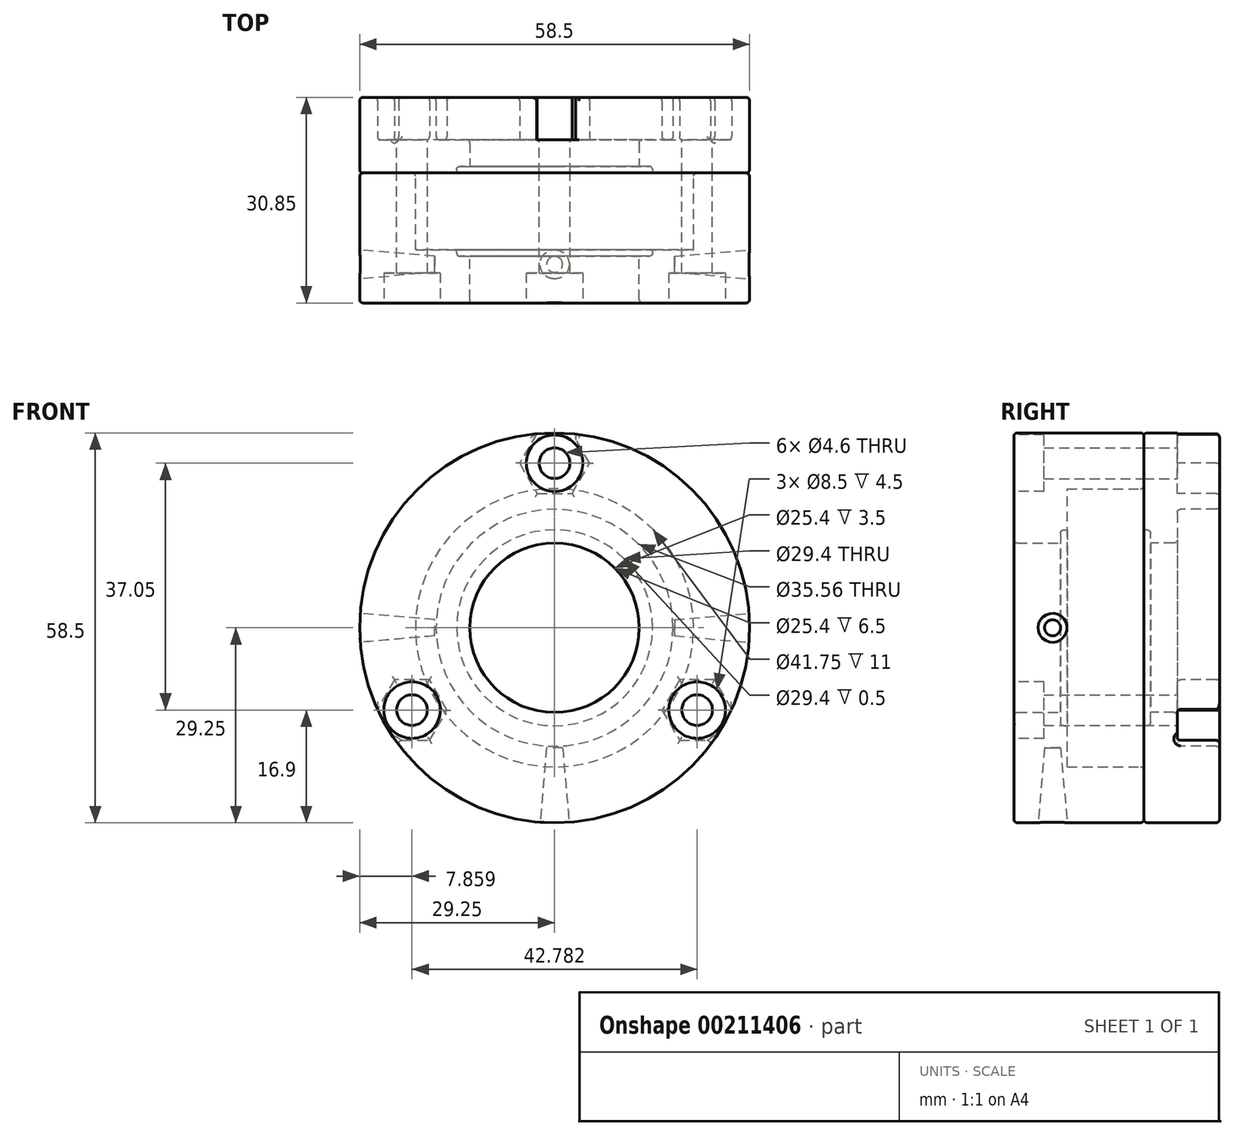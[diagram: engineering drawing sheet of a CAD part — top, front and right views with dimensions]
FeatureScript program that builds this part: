
annotation { "Feature Type Name" : "Feature", "Feature Type Description" : "" }
export const myFeature = defineFeature(function(context is Context, id is Id, definition is map)
    precondition{}
    {
        {
            var Q0;
            Q0=qCreatedBy(makeId("Front.planeOp"),FACE);
            var sketch = newSketch(context, id + "F0", { "sketchPlane" : qUnion([Q0])});
            skCircle(sketch, "E0", {"center": v(0, 0) * mm, "radius": 20.88 * mm});
            skCircle(sketch, "E1", {"center": v(0, 0) * mm, "radius": 29.25 * mm});
            skSolve(sketch);
        }
        {
            var Q0;
            Q0 = qSketchRegion(id + "F0", true);
            extrude(context, id + "F1", {"entities" : qUnion([Q0]), "depth" : 11.5 * mm});
        }
        {
            var Q0;
            Q0=makeQuery(id+"F1.opExtrude","CAP_FACE",FACE,{"disambiguationData":[OSD([sQuery(id+"F0.wireOp",EDGE,"E0"),sQuery(id+"F0.wireOp",EDGE,"E1")])],"isStart":false});
            var sketch = newSketch(context, id + "F2", { "sketchPlane" : qUnion([Q0])});
            skCircle(sketch, "E2.0", {"center": v(0, 0) * mm, "radius": 29.25 * mm});
            skCircle(sketch, "E3", {"center": v(0, 0) * mm, "radius": 12.7 * mm});
            skSolve(sketch);
        }
        {
            var Q0;
            Q0 = qSketchRegion(id + "F2", true);
            extrude(context, id + "F3", {"entities" : qUnion([Q0]), "operationType" : NewBodyOperationType.ADD, "depth" : 8 * mm});
        }
        {
            var Q0;
            Q0=makeQuery(id+"F1.opExtrude","CAP_FACE",FACE,{"disambiguationData":[OSD([sQuery(id+"F0.wireOp",EDGE,"E0"),sQuery(id+"F0.wireOp",EDGE,"E1")])],"isStart":true});
            var sketch = newSketch(context, id + "F4", { "sketchPlane" : qUnion([Q0])});
            skCircle(sketch, "E4.0", {"center": v(0, 0) * mm, "radius": 29.25 * mm});
            skCircle(sketch, "E5.0", {"center": v(0, 0) * mm, "radius": 12.7 * mm});
            skSolve(sketch);
        }
        {
            var Q0;
            Q0 = qSketchRegion(id + "F4", true);
            extrude(context, id + "F5", {"entities" : qUnion([Q0]), "depth" : 5 * mm});
        }
        {
            var Q0;
            Q0=makeQuery(id+"F3.opExtrude","CAP_FACE",FACE,{"disambiguationData":[OSD([sQuery(id+"F2.wireOp",EDGE,"E2.0"),sQuery(id+"F2.wireOp",EDGE,"E3")])],"isStart":true});
            var sketch = newSketch(context, id + "F6", { "sketchPlane" : qUnion([Q0])});
            skCircle(sketch, "E6.0", {"center": v(0, 0) * mm, "radius": 12.7 * mm});
            skCircle(sketch, "E7.0", {"center": v(0, 0) * mm, "radius": 14.7 * mm});
            skSolve(sketch);
        }
        {
            var Q0;
            Q0 = qSketchRegion(id + "F6", true);
            extrude(context, id + "F7", {"entities" : qUnion([Q0]), "operationType" : NewBodyOperationType.REMOVE, "oppositeDirection" : true, "depth" : 1 * mm});
        }
        {
            var Q0;
            Q0=makeQuery(id+"F7.boolean.opBoolean","COPY",EDGE,{"derivedFrom":makeQuery(id+"F7.opExtrude","CAP_EDGE",EDGE,{"disambiguationData":[OSD([sQuery(id+"F6.wireOp",EDGE,"E7.0")])],"isStart":true})});
            var Q1;
            Q1=makeQuery(id+"F7.boolean.opBoolean","COPY",EDGE,{"derivedFrom":makeQuery(id+"F7.opExtrude","CAP_EDGE",EDGE,{"disambiguationData":[OSD([sQuery(id+"F6.wireOp",EDGE,"E7.0")])],"isStart":false})});
            fillet(context, id + "F8", {"entities" : qUnion([Q0, Q1]), "radius" : .5 * mm, "tangentPropagation" : true, "allowEdgeOverflow" : false});
        }
        {
            var Q0;
            Q0=makeQuery(id+"F7.boolean.opBoolean","COPY",EDGE,{"derivedFrom":makeQuery(id+"F7.opExtrude","CAP_EDGE",EDGE,{"disambiguationData":[OSD([sQuery(id+"F6.wireOp",EDGE,"E6.0")])],"isStart":false})});
            var Q1;
            Q1=makeQuery(id+"F3.opExtrude","CAP_EDGE",EDGE,{"disambiguationData":[OSD([sQuery(id+"F2.wireOp",EDGE,"E3")])],"isStart":false});
            var Q2;
            Q2=makeQuery(id+"F1.opExtrude","CAP_EDGE",EDGE,{"disambiguationData":[OSD([sQuery(id+"F0.wireOp",EDGE,"E1")])],"isStart":true});
            var Q3;
            Q3=makeQuery(id+"F3.opExtrude","CAP_EDGE",EDGE,{"disambiguationData":[OSD([sQuery(id+"F2.wireOp",EDGE,"E2.0")])],"isStart":false});
            fillet(context, id + "F9", {"entities" : qUnion([Q0, Q1, Q2, Q3]), "radius" : .5 * mm, "tangentPropagation" : true, "allowEdgeOverflow" : false});
        }
        {
            var Q0;
            Q0=makeQuery(id+"F1.opExtrude","CAP_EDGE",EDGE,{"disambiguationData":[OSD([sQuery(id+"F0.wireOp",EDGE,"E0")])],"isStart":false});
            var Q1;
            Q1=makeQuery(id+"F1.opExtrude","CAP_EDGE",EDGE,{"disambiguationData":[OSD([sQuery(id+"F0.wireOp",EDGE,"E0")])],"isStart":true});
            fillet(context, id + "F10", {"entities" : qUnion([Q0, Q1]), "radius" : .5 * mm, "tangentPropagation" : true, "allowEdgeOverflow" : false});
        }
        {
            var Q0;
            Q0=makeQuery(id+"F5.opExtrude","CAP_FACE",FACE,{"disambiguationData":[OSD([sQuery(id+"F4.wireOp",EDGE,"E4.0"),sQuery(id+"F4.wireOp",EDGE,"E5.0")])],"isStart":true});
            var sketch = newSketch(context, id + "F11", { "sketchPlane" : qUnion([Q0])});
            skCircle(sketch, "E8.0", {"center": v(0, 0) * mm, "radius": 14.7 * mm});
            skCircle(sketch, "E9.0", {"center": v(0, 0) * mm, "radius": 12.7 * mm});
            skSolve(sketch);
        }
        {
            var Q0;
            Q0 = qSketchRegion(id + "F11", true);
            extrude(context, id + "F12", {"entities" : qUnion([Q0]), "operationType" : NewBodyOperationType.REMOVE, "oppositeDirection" : true, "depth" : 1 * mm});
        }
        {
            var Q0;
            Q0=makeQuery(id+"F12.boolean.opBoolean","COPY",EDGE,{"derivedFrom":makeQuery(id+"F12.opExtrude","CAP_EDGE",EDGE,{"disambiguationData":[OSD([sQuery(id+"F11.wireOp",EDGE,"E8.0")])],"isStart":false})});
            var Q1;
            Q1=makeQuery(id+"F12.boolean.opBoolean","COPY",EDGE,{"derivedFrom":makeQuery(id+"F12.opExtrude","CAP_EDGE",EDGE,{"disambiguationData":[OSD([sQuery(id+"F11.wireOp",EDGE,"E9.0")])],"isStart":false})});
            var Q2;
            Q2=makeQuery(id+"F12.boolean.opBoolean","COPY",EDGE,{"derivedFrom":makeQuery(id+"F12.opExtrude","CAP_EDGE",EDGE,{"disambiguationData":[OSD([sQuery(id+"F11.wireOp",EDGE,"E8.0")])],"isStart":true})});
            var Q3;
            Q3=makeQuery(id+"F5.opExtrude","CAP_EDGE",EDGE,{"disambiguationData":[OSD([sQuery(id+"F4.wireOp",EDGE,"E5.0")])],"isStart":false});
            var Q4;
            Q4=makeQuery(id+"F5.opExtrude","CAP_EDGE",EDGE,{"disambiguationData":[OSD([sQuery(id+"F4.wireOp",EDGE,"E4.0")])],"isStart":true});
            fillet(context, id + "F13", {"entities" : qUnion([Q0, Q1, Q2, Q3, Q4]), "radius" : .5 * mm, "tangentPropagation" : true, "allowEdgeOverflow" : false});
        }
        {
            var Q0;
            Q0=makeQuery(id+"F5.opExtrude","CAP_FACE",FACE,{"disambiguationData":[OSD([sQuery(id+"F4.wireOp",EDGE,"E4.0"),sQuery(id+"F4.wireOp",EDGE,"E5.0")])],"isStart":false});
            var sketch = newSketch(context, id + "F14", { "sketchPlane" : qUnion([Q0])});
            skPoint(sketch, "E10", {"position": v(0, 24.7) * mm});
            skCircle(sketch, "E11.0", {"center": v(0, 0) * mm, "radius": 20.88 * mm, "construction": true});
            skPoint(sketch, "E12.1.0", {"position": v(-21.4, -12.35) * mm});
            skPoint(sketch, "E12.2.0", {"position": v(21.4, -12.35) * mm});
            skSolve(sketch);
        }
        {
            var Q0;
            Q0=sQuery(id+"F14.wireOp",VERTEX,"E10");
            var Q1;
            Q1=sQuery(id+"F14.wireOp",VERTEX,"E12.2.0");
            var Q2;
            Q2=sQuery(id+"F14.wireOp",VERTEX,"E12.1.0");
            var Q3;
            Q3=makeQuery(id+"F1.opExtrude","SWEPT_BODY",BODY,{"disambiguationData":[OSD([sQuery(id+"F0.wireOp",EDGE,"E0"),sQuery(id+"F0.wireOp",EDGE,"E1")])]});
            var Q4;
            Q4=makeQuery(id+"F5.opExtrude","SWEPT_BODY",BODY,{"disambiguationData":[OSD([sQuery(id+"F4.wireOp",EDGE,"E4.0"),sQuery(id+"F4.wireOp",EDGE,"E5.0")])]});
            hole(context, id + "F15", {"style" : HoleStyle.SIMPLE, "endStyle" : HoleEndStyle.THROUGH, "holeDiameter" : 4.6 * mm, "locations" : qUnion([Q0, Q1, Q2]), "scope" : qUnion([Q3, Q4]), "isTappedThrough" : true});
        }
        {
            var Q0;
            Q0=makeQuery(id+"F3.opExtrude","CAP_FACE",FACE,{"disambiguationData":[OSD([sQuery(id+"F2.wireOp",EDGE,"E2.0"),sQuery(id+"F2.wireOp",EDGE,"E3")])],"isStart":false});
            var sketch = newSketch(context, id + "F16", { "sketchPlane" : qUnion([Q0])});
            skPoint(sketch, "E13.0", {"position": v(0, 24.7) * mm});
            skCircle(sketch, "E13.1", {"center": v(0, 0) * mm, "radius": 20.88 * mm, "construction": true});
            skPoint(sketch, "E13.2", {"position": v(21.4, -12.35) * mm});
            skPoint(sketch, "E13.3", {"position": v(-21.4, -12.35) * mm});
            skPoint(sketch, "E13.4", {"position": v(0, 0) * mm});
            skSolve(sketch);
        }
        {
            var Q0;
            Q0=makeQuery(id+"F5.opExtrude","CAP_FACE",FACE,{"disambiguationData":[OSD([sQuery(id+"F4.wireOp",EDGE,"E4.0"),sQuery(id+"F4.wireOp",EDGE,"E5.0")])],"isStart":false});
            var sketch = newSketch(context, id + "F17", { "sketchPlane" : qUnion([Q0])});
            skCircle(sketch, "E14.cCircle", {"center": v(0, 24.7) * mm, "radius": 4.55 * mm, "construction": true});
            skLineSegment(sketch, "E14.0", {"start": v(-2.63, 20.15) * mm, "end": v(-5.25, 24.7) * mm});
            skLineSegment(sketch, "E14.1", {"start": v(-5.25, 24.7) * mm, "end": v(-2.63, 29.25) * mm});
            skLineSegment(sketch, "E14.2", {"start": v(-2.63, 29.25) * mm, "end": v(2.63, 29.25) * mm});
            skLineSegment(sketch, "E14.3", {"start": v(2.63, 29.25) * mm, "end": v(5.25, 24.7) * mm});
            skLineSegment(sketch, "E14.4", {"start": v(5.25, 24.7) * mm, "end": v(2.63, 20.15) * mm});
            skLineSegment(sketch, "E14.5", {"start": v(2.63, 20.15) * mm, "end": v(-2.63, 20.15) * mm});
            skPoint(sketch, "E14.0.midPoint", {"position": v(-3.94, 22.42) * mm});
            skLineSegment(sketch, "E15.1.0", {"start": v(-26.64, -12.35) * mm, "end": v(-24.02, -7.8) * mm});
            skLineSegment(sketch, "E15.1.1", {"start": v(-24.02, -7.8) * mm, "end": v(-18.76, -7.8) * mm});
            skLineSegment(sketch, "E15.1.2", {"start": v(-18.76, -7.8) * mm, "end": v(-16.14, -12.35) * mm});
            skLineSegment(sketch, "E15.1.3", {"start": v(-16.14, -12.35) * mm, "end": v(-18.76, -16.9) * mm});
            skLineSegment(sketch, "E15.1.4", {"start": v(-18.76, -16.9) * mm, "end": v(-24.02, -16.9) * mm});
            skLineSegment(sketch, "E15.1.5", {"start": v(-24.02, -16.9) * mm, "end": v(-26.64, -12.35) * mm});
            skLineSegment(sketch, "E15.2.0", {"start": v(24.02, -16.9) * mm, "end": v(18.76, -16.9) * mm});
            skLineSegment(sketch, "E15.2.1", {"start": v(18.76, -16.9) * mm, "end": v(16.14, -12.35) * mm});
            skLineSegment(sketch, "E15.2.2", {"start": v(16.14, -12.35) * mm, "end": v(18.76, -7.8) * mm});
            skLineSegment(sketch, "E15.2.3", {"start": v(18.76, -7.8) * mm, "end": v(24.02, -7.8) * mm});
            skLineSegment(sketch, "E15.2.4", {"start": v(24.02, -7.8) * mm, "end": v(26.64, -12.35) * mm});
            skLineSegment(sketch, "E15.2.5", {"start": v(26.64, -12.35) * mm, "end": v(24.02, -16.9) * mm});
            skPoint(sketch, "E15.center", {"position": v(0, 0) * mm});
            skArc(sketch, "E16.0", {"start": v(-23.87, -16.9) * mm, "mid": v(0, -29.25) * mm, "end": v(23.87, -16.9) * mm});
            skArc(sketch, "E17.trimOffspring", {"start": v(26.57, -12.23) * mm, "mid": v(25.33, 14.62) * mm, "end": v(2.7, 29.13) * mm});
            skArc(sketch, "E18.trimOffspring", {"start": v(-2.7, 29.13) * mm, "mid": v(-25.33, 14.63) * mm, "end": v(-26.57, -12.23) * mm});
            skCircle(sketch, "E19", {"center": v(0, 0) * mm, "radius": 17.78 * mm});
            skSolve(sketch);
        }
        {
            var Q0;
            {var subQ8=sQuery(id+"F17.wireOp",EDGE,"E14.0");Q0=makeQuery(id+"F17.imprint","IMPRINT",FACE,{"disambiguationData":[TD([[makeQuery(id+"F17.imprint","IMPRINT",EDGE,{"derivedFrom":subQ8}),1.0]])]});}
            extrude(context, id + "F18", {"entities" : qUnion([Q0]), "operationType" : NewBodyOperationType.ADD, "depth" : 6.35 * mm});
        }
        {
            var Q0;
            Q0=makeQuery(id+"F18.opExtrude","CAP_EDGE",EDGE,{"disambiguationData":[OSD([sQuery(id+"F17.wireOp",EDGE,"E19")])],"isStart":true});
            var Q1;
            Q1=makeQuery(id+"F18.opExtrude","CAP_EDGE",EDGE,{"disambiguationData":[OSD([sQuery(id+"F17.wireOp",EDGE,"E19")])],"isStart":false});
            var Q2;
            Q2=makeQuery(id+"F18.opExtrude","CAP_EDGE",EDGE,{"disambiguationData":[OSD([sQuery(id+"F17.wireOp",EDGE,"E17.trimOffspring")])],"isStart":false});
            var Q3;
            Q3=makeQuery(id+"F18.opExtrude","CAP_EDGE",EDGE,{"disambiguationData":[OSD([sQuery(id+"F17.wireOp",EDGE,"E18.trimOffspring")])],"isStart":false});
            var Q4;
            Q4=makeQuery(id+"F18.opExtrude","CAP_EDGE",EDGE,{"disambiguationData":[OSD([sQuery(id+"F17.wireOp",EDGE,"E16.0")])],"isStart":false});
            var Q5;
            Q5=makeQuery(id+"F18.opExtrude","CAP_EDGE",EDGE,{"disambiguationData":[OSD([sQuery(id+"F17.wireOp",EDGE,"E15.1.4")])],"isStart":false});
            var Q6;
            Q6=makeQuery(id+"F18.opExtrude","CAP_EDGE",EDGE,{"disambiguationData":[OSD([sQuery(id+"F17.wireOp",EDGE,"E15.1.3")])],"isStart":false});
            var Q7;
            Q7=makeQuery(id+"F18.opExtrude","CAP_EDGE",EDGE,{"disambiguationData":[OSD([sQuery(id+"F17.wireOp",EDGE,"E15.1.2")])],"isStart":false});
            var Q8;
            Q8=makeQuery(id+"F18.opExtrude","CAP_EDGE",EDGE,{"disambiguationData":[OSD([sQuery(id+"F17.wireOp",EDGE,"E15.1.1")])],"isStart":false});
            var Q9;
            Q9=makeQuery(id+"F18.opExtrude","CAP_EDGE",EDGE,{"disambiguationData":[OSD([sQuery(id+"F17.wireOp",EDGE,"E15.1.0")])],"isStart":false});
            var Q10;
            Q10=makeQuery(id+"F18.opExtrude","CAP_EDGE",EDGE,{"disambiguationData":[OSD([sQuery(id+"F17.wireOp",EDGE,"E15.2.0")])],"isStart":false});
            var Q11;
            Q11=makeQuery(id+"F18.opExtrude","CAP_EDGE",EDGE,{"disambiguationData":[OSD([sQuery(id+"F17.wireOp",EDGE,"E15.2.1")])],"isStart":false});
            var Q12;
            Q12=makeQuery(id+"F18.opExtrude","CAP_EDGE",EDGE,{"disambiguationData":[OSD([sQuery(id+"F17.wireOp",EDGE,"E15.2.2")])],"isStart":false});
            var Q13;
            Q13=makeQuery(id+"F18.opExtrude","CAP_EDGE",EDGE,{"disambiguationData":[OSD([sQuery(id+"F17.wireOp",EDGE,"E15.2.3")])],"isStart":false});
            var Q14;
            Q14=makeQuery(id+"F18.opExtrude","CAP_EDGE",EDGE,{"disambiguationData":[OSD([sQuery(id+"F17.wireOp",EDGE,"E15.2.4")])],"isStart":false});
            var Q15;
            Q15=makeQuery(id+"F18.opExtrude","CAP_EDGE",EDGE,{"disambiguationData":[OSD([sQuery(id+"F17.wireOp",EDGE,"E14.4")])],"isStart":false});
            var Q16;
            Q16=makeQuery(id+"F18.opExtrude","CAP_EDGE",EDGE,{"disambiguationData":[OSD([sQuery(id+"F17.wireOp",EDGE,"E14.3")])],"isStart":false});
            var Q17;
            Q17=makeQuery(id+"F18.opExtrude","CAP_EDGE",EDGE,{"disambiguationData":[OSD([sQuery(id+"F17.wireOp",EDGE,"E14.5")])],"isStart":false});
            var Q18;
            Q18=makeQuery(id+"F18.opExtrude","CAP_EDGE",EDGE,{"disambiguationData":[OSD([sQuery(id+"F17.wireOp",EDGE,"E14.0")])],"isStart":false});
            var Q19;
            Q19=makeQuery(id+"F18.opExtrude","CAP_EDGE",EDGE,{"disambiguationData":[OSD([sQuery(id+"F17.wireOp",EDGE,"E14.1")])],"isStart":false});
            var Q20;
            Q20=makeQuery(id+"F18.opExtrude","CAP_EDGE",EDGE,{"disambiguationData":[OSD([sQuery(id+"F17.wireOp",EDGE,"E14.4")])],"isStart":true});
            var Q21;
            Q21=makeQuery(id+"F18.opExtrude","CAP_EDGE",EDGE,{"disambiguationData":[OSD([sQuery(id+"F17.wireOp",EDGE,"E14.3")])],"isStart":true});
            var Q22;
            Q22=makeQuery(id+"F18.opExtrude","CAP_EDGE",EDGE,{"disambiguationData":[OSD([sQuery(id+"F17.wireOp",EDGE,"E14.1")])],"isStart":true});
            var Q23;
            Q23=makeQuery(id+"F18.opExtrude","CAP_EDGE",EDGE,{"disambiguationData":[OSD([sQuery(id+"F17.wireOp",EDGE,"E14.0")])],"isStart":true});
            var Q24;
            Q24=makeQuery(id+"F18.opExtrude","CAP_EDGE",EDGE,{"disambiguationData":[OSD([sQuery(id+"F17.wireOp",EDGE,"E14.5")])],"isStart":true});
            var Q25;
            Q25=makeQuery(id+"F18.opExtrude","CAP_EDGE",EDGE,{"disambiguationData":[OSD([sQuery(id+"F17.wireOp",EDGE,"E15.2.3")])],"isStart":true});
            var Q26;
            Q26=makeQuery(id+"F18.opExtrude","CAP_EDGE",EDGE,{"disambiguationData":[OSD([sQuery(id+"F17.wireOp",EDGE,"E15.2.2")])],"isStart":true});
            var Q27;
            Q27=makeQuery(id+"F18.opExtrude","CAP_EDGE",EDGE,{"disambiguationData":[OSD([sQuery(id+"F17.wireOp",EDGE,"E15.2.1")])],"isStart":true});
            var Q28;
            Q28=makeQuery(id+"F18.opExtrude","CAP_EDGE",EDGE,{"disambiguationData":[OSD([sQuery(id+"F17.wireOp",EDGE,"E15.2.0")])],"isStart":true});
            var Q29;
            Q29=makeQuery(id+"F18.opExtrude","CAP_EDGE",EDGE,{"disambiguationData":[OSD([sQuery(id+"F17.wireOp",EDGE,"E15.2.4")])],"isStart":true});
            var Q30;
            Q30=makeQuery(id+"F18.opExtrude","CAP_EDGE",EDGE,{"disambiguationData":[OSD([sQuery(id+"F17.wireOp",EDGE,"E15.1.2")])],"isStart":true});
            var Q31;
            Q31=makeQuery(id+"F18.opExtrude","CAP_EDGE",EDGE,{"disambiguationData":[OSD([sQuery(id+"F17.wireOp",EDGE,"E15.1.3")])],"isStart":true});
            var Q32;
            Q32=makeQuery(id+"F18.opExtrude","CAP_EDGE",EDGE,{"disambiguationData":[OSD([sQuery(id+"F17.wireOp",EDGE,"E15.1.1")])],"isStart":true});
            var Q33;
            Q33=makeQuery(id+"F18.opExtrude","CAP_EDGE",EDGE,{"disambiguationData":[OSD([sQuery(id+"F17.wireOp",EDGE,"E15.1.0")])],"isStart":true});
            var Q34;
            Q34=makeQuery(id+"F18.opExtrude","CAP_EDGE",EDGE,{"disambiguationData":[OSD([sQuery(id+"F17.wireOp",EDGE,"E15.1.4")])],"isStart":true});
            var Q35;
            Q35=makeQuery(id+"F18.opExtrude","SWEPT_EDGE",EDGE,{"disambiguationData":[OSD([sQuery(id+"F4.wireOp",EDGE,"E4.0"),sQuery(id+"F17.wireOp",EDGE,"E14.1"),sQuery(id+"F17.wireOp",EDGE,"E18.trimOffspring")])]});
            var Q36;
            Q36=makeQuery(id+"F18.opExtrude","SWEPT_EDGE",EDGE,{"disambiguationData":[OSD([sQuery(id+"F4.wireOp",EDGE,"E4.0"),sQuery(id+"F17.wireOp",EDGE,"E15.2.0"),sQuery(id+"F17.wireOp",EDGE,"E16.0")])]});
            var Q37;
            Q37=makeQuery(id+"F18.opExtrude","SWEPT_EDGE",EDGE,{"disambiguationData":[OSD([sQuery(id+"F4.wireOp",EDGE,"E4.0"),sQuery(id+"F17.wireOp",EDGE,"E15.1.4"),sQuery(id+"F17.wireOp",EDGE,"E16.0")])]});
            fillet(context, id + "F19", {"entities" : qUnion([Q0, Q1, Q2, Q3, Q4, Q5, Q6, Q7, Q8, Q9, Q10, Q11, Q12, Q13, Q14, Q15, Q16, Q17, Q18, Q19, Q20, Q21, Q22, Q23, Q24, Q25, Q26, Q27, Q28, Q29, Q30, Q31, Q32, Q33, Q34, Q35, Q36, Q37]), "radius" : .5 * mm, "tangentPropagation" : true, "allowEdgeOverflow" : false});
        }
        {
            var Q0;
            Q0=makeQuery(id+"F3.opExtrude","CAP_FACE",FACE,{"disambiguationData":[OSD([sQuery(id+"F2.wireOp",EDGE,"E2.0"),sQuery(id+"F2.wireOp",EDGE,"E3")])],"isStart":false});
            var sketch = newSketch(context, id + "F20", { "sketchPlane" : qUnion([Q0])});
            skCircle(sketch, "E20.0", {"center": v(21.4, -12.35) * mm, "radius": 4.25 * mm});
            skCircle(sketch, "E20.2", {"center": v(-21.4, -12.35) * mm, "radius": 4.25 * mm});
            skCircle(sketch, "E21", {"center": v(0, 24.7) * mm, "radius": 4.25 * mm});
            skSolve(sketch);
        }
        {
            var Q0;
            Q0 = qSketchRegion(id + "F20", true);
            extrude(context, id + "F21", {"entities" : qUnion([Q0]), "operationType" : NewBodyOperationType.REMOVE, "oppositeDirection" : true, "depth" : 4.5 * mm});
        }
        {
            var Q0;
            Q0=qCreatedBy(makeId("Right.planeOp"),FACE);
            cPlane(context, id + "F22", {"entities" : qUnion([Q0]), "cplaneType" : CPlaneType.OFFSET, "offset" : 30 * mm, "width" : 150 * mm, "height" : 150 * mm});
        }
        {
            var Q0;
            Q0=qCreatedBy(makeId("Right.planeOp"),FACE);
            cPlane(context, id + "F23", {"entities" : qUnion([Q0]), "cplaneType" : CPlaneType.OFFSET, "offset" : 30 * mm, "oppositeDirection" : true, "width" : 150 * mm, "height" : 150 * mm});
        }
        {
            var Q0;
            Q0=qCreatedBy(makeId("Top.planeOp"),FACE);
            cPlane(context, id + "F24", {"entities" : qUnion([Q0]), "cplaneType" : CPlaneType.OFFSET, "offset" : 30 * mm, "oppositeDirection" : true, "width" : 150 * mm, "height" : 150 * mm});
        }
        {
            var Q0;
            Q0=qCreatedBy(id+"F22.planeOp",FACE);
            var sketch = newSketch(context, id + "F25", { "sketchPlane" : qUnion([Q0])});
            skCircle(sketch, "E22", {"center": v(-13.7, 0) * mm, "radius": 2.25 * mm});
            skSolve(sketch);
        }
        {
            var Q0;
            Q0=makeQuery(id+"F25.imprint","IMPRINT",FACE,{"disambiguationData":[TD([[makeQuery(id+"F25.imprint","IMPRINT",EDGE,{"derivedFrom":sQuery(id+"F25.wireOp",EDGE,"E22")}),1.0]])]});
            extrude(context, id + "F26", {"entities" : qUnion([Q0]), "operationType" : NewBodyOperationType.REMOVE, "oppositeDirection" : true, "depth" : 12 * mm, "hasDraft" : true, "draftAngle" : 5 * degree, "draftPullDirection" : true});
        }
        {
            var Q0;
            Q0=qCreatedBy(id+"F23.planeOp",FACE);
            var sketch = newSketch(context, id + "F27", { "sketchPlane" : qUnion([Q0])});
            skCircle(sketch, "E23.0", {"center": v(-13.7, 0) * mm, "radius": 2.25 * mm});
            skSolve(sketch);
        }
        {
            var Q0;
            Q0 = qSketchRegion(id + "F27", true);
            extrude(context, id + "F28", {"entities" : qUnion([Q0]), "operationType" : NewBodyOperationType.REMOVE, "depth" : 12 * mm, "hasDraft" : true, "draftAngle" : 5 * degree, "draftPullDirection" : true});
        }
        {
            var Q0;
            Q0=qCreatedBy(id+"F24.planeOp",FACE);
            var sketch = newSketch(context, id + "F29", { "sketchPlane" : qUnion([Q0])});
            skCircle(sketch, "E24", {"center": v(0, -13.7) * mm, "radius": 2.25 * mm});
            skSolve(sketch);
        }
        {
            var Q0;
            Q0 = qSketchRegion(id + "F29", true);
            extrude(context, id + "F30", {"entities" : qUnion([Q0]), "operationType" : NewBodyOperationType.REMOVE, "depth" : 12 * mm, "hasDraft" : true, "draftAngle" : 5 * degree, "draftPullDirection" : true});
        }
    });
